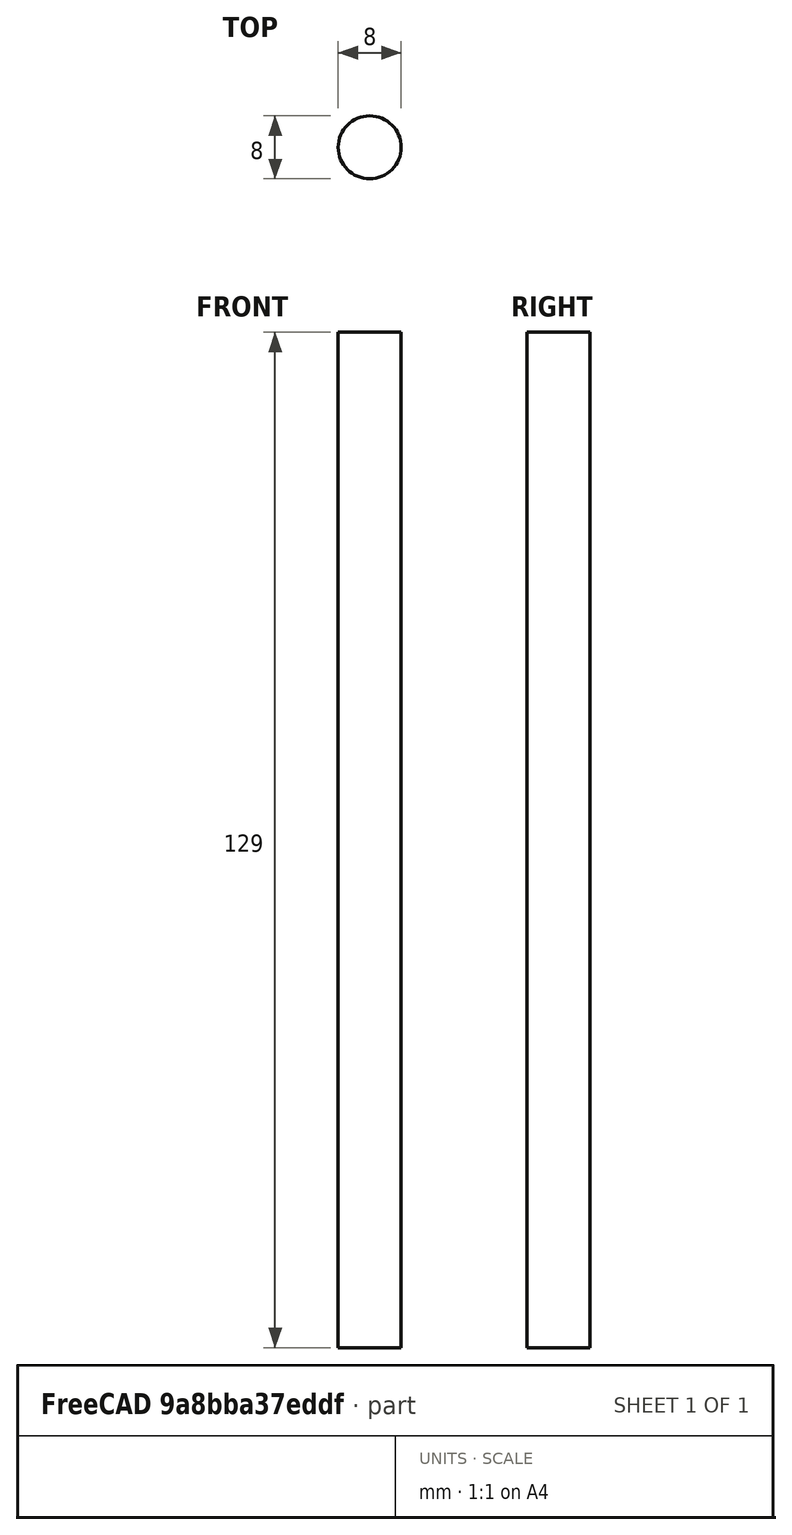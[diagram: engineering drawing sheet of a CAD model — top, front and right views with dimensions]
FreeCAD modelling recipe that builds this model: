
FCSTD DOCUMENT  (FreeCAD 1.0R39109 (Git))
Label: rod
License: All rights reserved
LicenseURL: https://en.wikipedia.org/wiki/All_rights_reserved
objects: Sketcher::SketchObject×1, PartDesign::Pad×1, PartDesign::Body×1
note: 6 computed .brp shape members not serialized (recipe doc carries the construction recipe); baked Part::Feature solids carry a one-line shape summary decoded from their .brp

FEATURE [Sketcher::SketchObject] Sketch
  ArcFitTolerance = 1e-06
  AttachmentSupport = -> [XY_Plane]
  FullyConstrained = true
  MakeInternals = false
  MapMode = 5
  sketch-geometry (1):
    g0: Circle CenterX=0 CenterY=0 CenterZ=0 NormalX=0 NormalY=0 NormalZ=1 AngleXU=0 Radius=4
  constraints (2):
    c: Diameter(g0) = 8
    c: Coincident(g0,g-1)
FEATURE [PartDesign::Pad] Pad
  Direction = (0,0,1)
  Length = 129
  Length2 = 10
  Profile = -> Sketch
  ReferenceAxis = -> Sketch [N_Axis]
  Refine = true
  Suppressed = false
  Type = 0
FEATURE [PartDesign::Body] Body
  AllowCompound = false
  Group = -> [Sketch,Pad]
  Origin = -> Origin
  Tip = -> Pad
